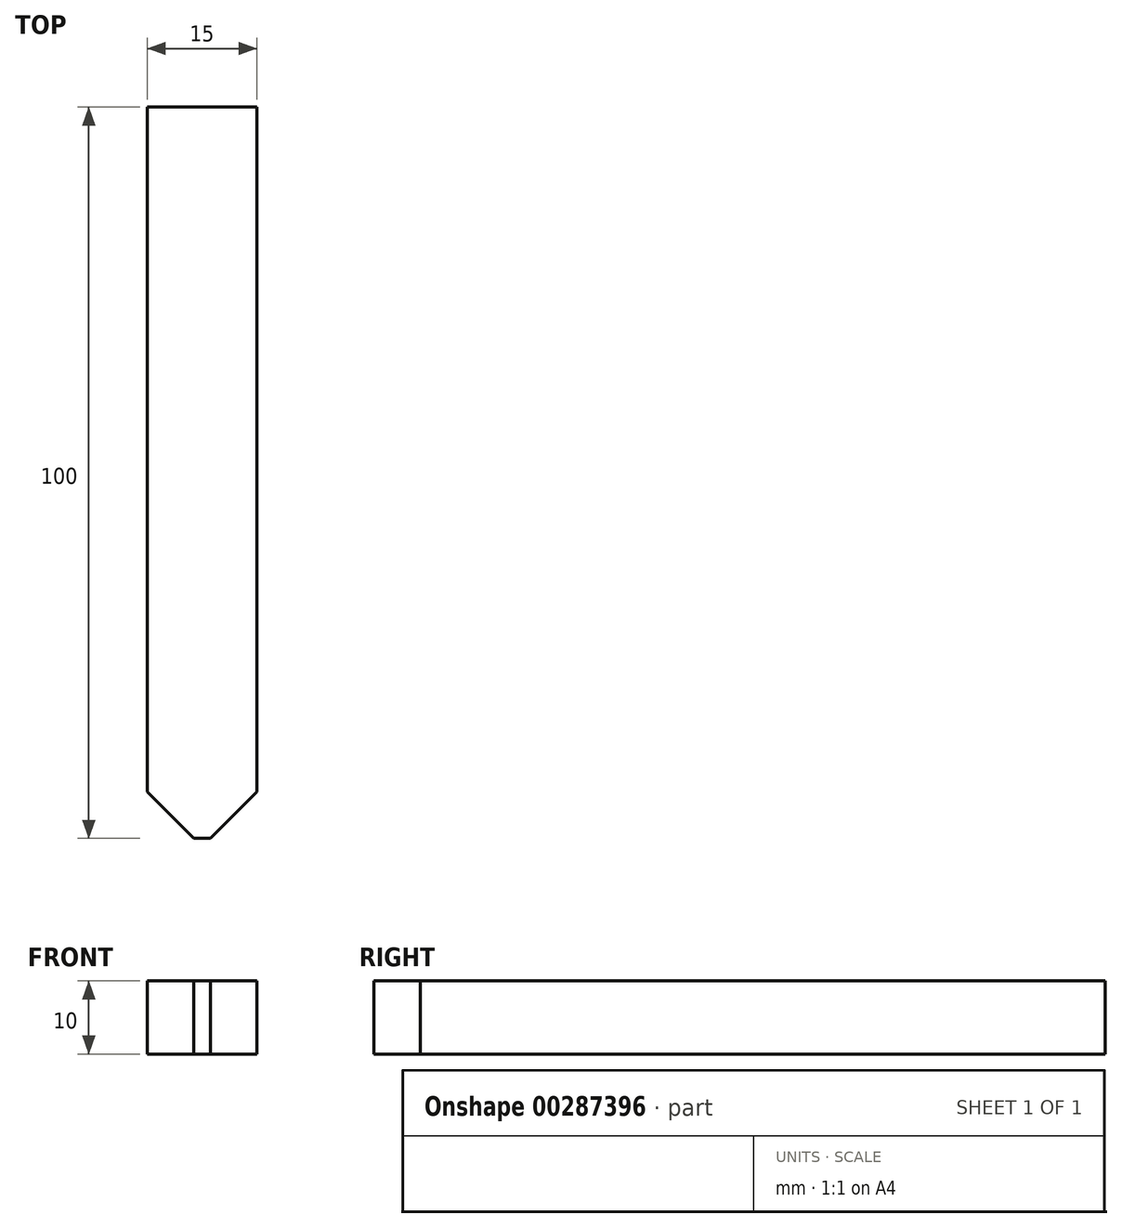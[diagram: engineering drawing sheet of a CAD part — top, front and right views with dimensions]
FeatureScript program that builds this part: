
annotation { "Feature Type Name" : "Feature", "Feature Type Description" : "" }
export const myFeature = defineFeature(function(context is Context, id is Id, definition is map)
    precondition{}
    {
        {
            var Q0;
            Q0=qCreatedBy(makeId("Top.planeOp"),FACE);
            var sketch = newSketch(context, id + "F0", { "sketchPlane" : qUnion([Q0])});
            skLineSegment(sketch, "E0.bottom", {"start": v(7.5, 50) * mm, "end": v(-7.5, 50) * mm});
            skLineSegment(sketch, "E0.top", {"start": v(7.5, -50) * mm, "end": v(-7.5, -50) * mm});
            skLineSegment(sketch, "E0.left", {"start": v(7.5, 50) * mm, "end": v(7.5, -50) * mm});
            skLineSegment(sketch, "E0.right", {"start": v(-7.5, 50) * mm, "end": v(-7.5, -50) * mm});
            skPoint(sketch, "E0.middle", {"position": v(0, 0) * mm});
            skSolve(sketch);
        }
        {
            var Q0;
            Q0=makeQuery(id+"F0.imprint","IMPRINT",FACE,{"disambiguationData":[TD([[makeQuery(id+"F0.imprint","IMPRINT",EDGE,{"derivedFrom":sQuery(id+"F0.wireOp",EDGE,"E0.bottom")}),1.0]])]});
            extrude(context, id + "F1", {"entities" : qUnion([Q0]), "depth" : 10 * mm});
        }
        {
            var Q0;
            Q0=makeQuery(id+"F1.opExtrude","SWEPT_EDGE",EDGE,{"disambiguationData":[OSD([sQuery(id+"F0.wireOp",EDGE,"E0.top"),sQuery(id+"F0.wireOp",EDGE,"E0.right")])]});
            var Q1;
            Q1=makeQuery(id+"F1.opExtrude","SWEPT_EDGE",EDGE,{"disambiguationData":[OSD([sQuery(id+"F0.wireOp",EDGE,"E0.top"),sQuery(id+"F0.wireOp",EDGE,"E0.left")])]});
            chamfer(context, id + "F2", {"entities" : qUnion([Q0, Q1]), "width" : 6.35 * mm, "tangentPropagation" : true});
        }
    });
